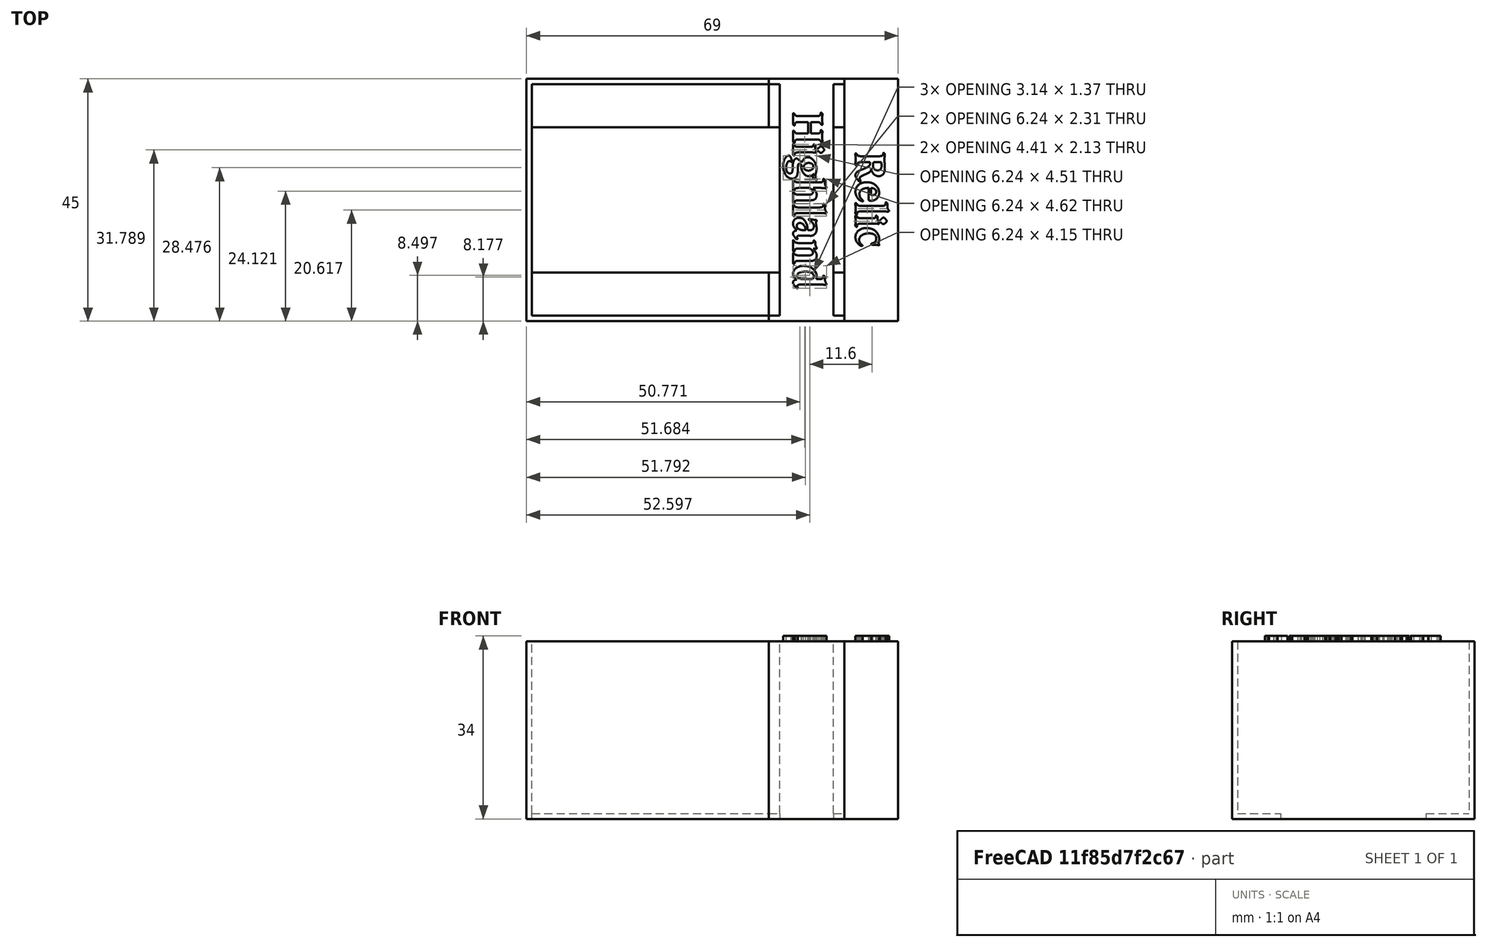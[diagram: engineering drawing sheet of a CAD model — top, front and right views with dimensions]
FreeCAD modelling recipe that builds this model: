
FCSTD DOCUMENT  (FreeCAD 0.18.4R)
Label: test
License: All rights reserved
LicenseURL: http://en.wikipedia.org/wiki/All_rights_reserved
objects: Part::FeaturePython×28, Part::Box×10, Part::MultiFuse×6, Part::Cut×4, Part::Part2DObjectPython×2, Part::Extrusion×2, Part::Feature×2, Part::Plane×2, App::DocumentObjectGroup×2
note: 56 computed .brp shape members not serialized (recipe doc carries the construction recipe); baked Part::Feature solids carry a one-line shape summary decoded from their .brp

FEATURE [Part::Box] Box  label="Cube"
  AttacherType = Attacher::AttachEngine3D
  Height = 33
  Length = 202
  Placement = pos=(0,-1,0) rot=(0,0,1;0rad)
  Width = 45
FEATURE [Part::Box] Box001  label="Cube001"
  AttacherType = Attacher::AttachEngine3D
  Height = 33
  Length = 200
  Placement = pos=(1,0,0) rot=(0,0,1;0rad)
  Width = 43
FEATURE [Part::Cut] Cut
  Base = -> Box
  Tool = -> Box001
FEATURE [Part::Box] Box002  label="Cube002"
  AttacherType = Attacher::AttachEngine3D
  Height = 1
  Length = 202
  Width = 8
FEATURE [Part::Box] Box003  label="Cube003"
  AttacherType = Attacher::AttachEngine3D
  Height = 1
  Length = 202
  Placement = pos=(0,35,0) rot=(0,0,1;0rad)
  Width = 8
FEATURE [Part::MultiFuse] Fusion
  Shapes = -> [Cut,Box002,Box003]
FEATURE [Part::Box] Box004  label="Cube004"
  AttacherType = Attacher::AttachEngine3D
  Height = 33
  Length = 10
  Placement = pos=(47,0,0) rot=(0,0,1;0rad)
  Width = 43
FEATURE [Part::Box] Box005  label="Cube005"
  AttacherType = Attacher::AttachEngine3D
  Height = 33
  Length = 10
  Placement = pos=(60,0,0) rot=(0,0,1;0rad)
  Width = 43
FEATURE [Part::Box] Box006  label="Cube006"
  AttacherType = Attacher::AttachEngine3D
  Height = 33
  Length = 141
  Placement = pos=(61,-1,0) rot=(0,0,1;0rad)
  Width = 45
FEATURE [Part::MultiFuse] Fusion001
  Shapes = -> [Fusion,Box004,Box005]
FEATURE [Part::Cut] Cut001
  Base = -> Fusion001
  Tool = -> Box006
FEATURE [Part::Box] Box007  label="Cube007"
  AttacherType = Attacher::AttachEngine3D
  Height = 33
  Length = 10
  Placement = pos=(59,-1,0) rot=(0,0,1;0rad)
  Width = 45
FEATURE [Part::MultiFuse] Fusion002
  Shapes = -> [Cut001,Box007]
FEATURE [Part::Part2DObjectPython] ShapeString  # Draft 2D object (typed FeaturePython)
  FontFile = <userpath>/Downloads/talisman/Caxton Bold.otf
  Placement = pos=(50.19,26.13,33) rot=(0,0,1;0rad)
  Size = 3
  String = Highland
  Tracking = 0
FEATURE [Part::Part2DObjectPython] ShapeString001  # Draft 2D object (typed FeaturePython)
  FontFile = <userpath>/Downloads/talisman/Caxton Bold.otf
  Placement = pos=(52.65,7.23,33) rot=(0,0,1;0rad)
  Size = 3
  String = Relic
  Tracking = 0
FEATURE [Part::Extrusion] Extrude
  Base = -> ShapeString
  Dir = (0,0,1)
  DirMode = 2
  FaceMakerClass = Part::FaceMakerBullseye
  LengthFwd = 1
  LengthRev = 0
  Placement = pos=(23.5,88,0) rot=(0,0,-1;1.5708rad)
  Solid = false
  Symmetric = false
FEATURE [Part::Extrusion] Extrude001
  Base = -> ShapeString001
  Dir = (0,0,1)
  DirMode = 2
  FaceMakerClass = Part::FaceMakerBullseye
  LengthFwd = 1
  LengthRev = 0
  Placement = pos=(54,83,0) rot=(0,0,-1;1.5708rad)
  Solid = false
  Symmetric = false
FEATURE [Part::MultiFuse] Fusion003
  Shapes = -> [Extrude001,Extrude,Fusion002]
FEATURE [Part::Feature] Fusion003001  label="Fusion004"
  shape: bbox 69 x 45 x 34 mm, 374 faces (baked)
FEATURE [Part::Plane] Plane001
  AttacherType = Attacher::AttachEngine3D
  Length = 100
  Placement = pos=(-10,-10,33) rot=(0,0,1;0rad)
  Width = 100
FEATURE [Part::FeaturePython] Slice  # WARN: FeaturePython — macro-defined, semantics opaque (R4)
  Base = -> Fusion003001
  Mode = 1
  Tolerance = 0
  Tools = -> [Plane001]
FEATURE [Part::FeaturePython] Slice_child0  label="Slice.0"  # WARN: FeaturePython — macro-defined, semantics opaque (R4)
  Base = -> Slice
  FilterType = 1
  Invert = false
  OverrideMaxVal = 0
  WindowFrom = 80
  WindowTo = 100
  items = 0
FEATURE [Part::FeaturePython] Slice_child1  label="Slice.1"  # WARN: FeaturePython — macro-defined, semantics opaque (R4)
  Base = -> Slice
  FilterType = 1
  Invert = false
  OverrideMaxVal = 0
  WindowFrom = 80
  WindowTo = 100
  items = 1
FEATURE [Part::FeaturePython] Slice_child2  label="Slice.2"  # WARN: FeaturePython — macro-defined, semantics opaque (R4)
  Base = -> Slice
  FilterType = 1
  Invert = false
  OverrideMaxVal = 0
  WindowFrom = 80
  WindowTo = 100
  items = 2
FEATURE [Part::FeaturePython] Slice_child3  label="Slice.3"  # WARN: FeaturePython — macro-defined, semantics opaque (R4)
  Base = -> Slice
  FilterType = 1
  Invert = false
  OverrideMaxVal = 0
  WindowFrom = 80
  WindowTo = 100
  items = 3
FEATURE [Part::FeaturePython] Slice_child4  label="Slice.4"  # WARN: FeaturePython — macro-defined, semantics opaque (R4)
  Base = -> Slice
  FilterType = 1
  Invert = false
  OverrideMaxVal = 0
  WindowFrom = 80
  WindowTo = 100
  items = 4
FEATURE [Part::FeaturePython] Slice_child5  label="Slice.5"  # WARN: FeaturePython — macro-defined, semantics opaque (R4)
  Base = -> Slice
  FilterType = 1
  Invert = false
  OverrideMaxVal = 0
  WindowFrom = 80
  WindowTo = 100
  items = 5
FEATURE [Part::FeaturePython] Slice_child6  label="Slice.6"  # WARN: FeaturePython — macro-defined, semantics opaque (R4)
  Base = -> Slice
  FilterType = 1
  Invert = false
  OverrideMaxVal = 0
  WindowFrom = 80
  WindowTo = 100
  items = 6
FEATURE [Part::FeaturePython] Slice_child7  label="Slice.7"  # WARN: FeaturePython — macro-defined, semantics opaque (R4)
  Base = -> Slice
  FilterType = 1
  Invert = false
  OverrideMaxVal = 0
  WindowFrom = 80
  WindowTo = 100
  items = 7
FEATURE [Part::FeaturePython] Slice_child8  label="Slice.8"  # WARN: FeaturePython — macro-defined, semantics opaque (R4)
  Base = -> Slice
  FilterType = 1
  Invert = false
  OverrideMaxVal = 0
  WindowFrom = 80
  WindowTo = 100
  items = 8
FEATURE [Part::FeaturePython] Slice_child9  label="Slice.9"  # WARN: FeaturePython — macro-defined, semantics opaque (R4)
  Base = -> Slice
  FilterType = 1
  Invert = false
  OverrideMaxVal = 0
  WindowFrom = 80
  WindowTo = 100
  items = 9
FEATURE [Part::FeaturePython] Slice_child10  label="Slice.10"  # WARN: FeaturePython — macro-defined, semantics opaque (R4)
  Base = -> Slice
  FilterType = 1
  Invert = false
  OverrideMaxVal = 0
  WindowFrom = 80
  WindowTo = 100
  items = 10
FEATURE [Part::FeaturePython] Slice_child11  label="Slice.11"  # WARN: FeaturePython — macro-defined, semantics opaque (R4)
  Base = -> Slice
  FilterType = 1
  Invert = false
  OverrideMaxVal = 0
  WindowFrom = 80
  WindowTo = 100
  items = 11
FEATURE [Part::FeaturePython] Slice_child12  label="Slice.12"  # WARN: FeaturePython — macro-defined, semantics opaque (R4)
  Base = -> Slice
  FilterType = 1
  Invert = false
  OverrideMaxVal = 0
  WindowFrom = 80
  WindowTo = 100
  items = 12
FEATURE [Part::FeaturePython] Slice_child13  label="Slice.13"  # WARN: FeaturePython — macro-defined, semantics opaque (R4)
  Base = -> Slice
  FilterType = 1
  Invert = false
  OverrideMaxVal = 0
  WindowFrom = 80
  WindowTo = 100
  items = 13
FEATURE [Part::FeaturePython] Slice_child14  label="Slice.14"  # WARN: FeaturePython — macro-defined, semantics opaque (R4)
  Base = -> Slice
  FilterType = 1
  Invert = false
  OverrideMaxVal = 0
  WindowFrom = 80
  WindowTo = 100
  items = 14
FEATURE [Part::FeaturePython] Slice_child15  label="Slice.15"  # WARN: FeaturePython — macro-defined, semantics opaque (R4)
  Base = -> Slice
  FilterType = 1
  Invert = false
  OverrideMaxVal = 0
  WindowFrom = 80
  WindowTo = 100
  items = 15
FEATURE [Part::MultiFuse] Fusion003002
  Shapes = -> [Slice_child1,Slice_child3,Slice_child5,Slice_child4,Slice_child2,Slice_child14,Slice_child6,Slice_child13,Slice_child8,Slice_child7,Slice_child10,Slice_child11,Slice_child9,Slice_child15,Slice_child12]
FEATURE [App::DocumentObjectGroup] GrExplode_Slice  label="Exploded Slice"
  Group = -> [Slice_child0,Fusion003002]
FEATURE [Part::Feature] Fusion003003
  shape: bbox 69 x 45 x 34 mm, 406 faces (baked)
FEATURE [Part::Box] Box008  label="Cube008"
  AttacherType = Attacher::AttachEngine3D
  Height = 40
  Length = 100
  Placement = pos=(-55,-10,-4) rot=(0,0,1;0rad)
  Width = 100
FEATURE [Part::Box] Box009  label="Cube009"
  AttacherType = Attacher::AttachEngine3D
  Height = 40
  Length = 100
  Placement = pos=(59,-10,-4) rot=(0,0,1;0rad)
  Width = 100
FEATURE [Part::Cut] Cut002
  Base = -> Fusion003003
  Tool = -> Box008
FEATURE [Part::Cut] Cut003
  Base = -> Cut002
  Tool = -> Box009
FEATURE [Part::Plane] Plane
  AttacherType = Attacher::AttachEngine3D
  Length = 100
  Placement = pos=(0,-23,33) rot=(0,0,1;0rad)
  Width = 100
FEATURE [Part::FeaturePython] Slice001  # WARN: FeaturePython — macro-defined, semantics opaque (R4)
  Base = -> Cut003
  Mode = 1
  Tolerance = 0
  Tools = -> [Plane]
FEATURE [Part::FeaturePython] Slice001_child0  label="pieza"  # WARN: FeaturePython — macro-defined, semantics opaque (R4)
  Base = -> Slice001
  FilterType = 1
  Invert = false
  OverrideMaxVal = 0
  WindowFrom = 80
  WindowTo = 100
  items = 0
FEATURE [Part::FeaturePython] Slice001_child1  label="Slice001.1"  # WARN: FeaturePython — macro-defined, semantics opaque (R4)
  Base = -> Slice001
  FilterType = 1
  Invert = false
  OverrideMaxVal = 0
  WindowFrom = 80
  WindowTo = 100
  items = 1
FEATURE [Part::FeaturePython] Slice001_child2  label="Slice001.2"  # WARN: FeaturePython — macro-defined, semantics opaque (R4)
  Base = -> Slice001
  FilterType = 1
  Invert = false
  OverrideMaxVal = 0
  WindowFrom = 80
  WindowTo = 100
  items = 2
FEATURE [Part::FeaturePython] Slice001_child3  label="Slice001.3"  # WARN: FeaturePython — macro-defined, semantics opaque (R4)
  Base = -> Slice001
  FilterType = 1
  Invert = false
  OverrideMaxVal = 0
  WindowFrom = 80
  WindowTo = 100
  items = 3
FEATURE [Part::FeaturePython] Slice001_child4  label="Slice001.4"  # WARN: FeaturePython — macro-defined, semantics opaque (R4)
  Base = -> Slice001
  FilterType = 1
  Invert = false
  OverrideMaxVal = 0
  WindowFrom = 80
  WindowTo = 100
  items = 4
FEATURE [Part::FeaturePython] Slice001_child5  label="Slice001.5"  # WARN: FeaturePython — macro-defined, semantics opaque (R4)
  Base = -> Slice001
  FilterType = 1
  Invert = false
  OverrideMaxVal = 0
  WindowFrom = 80
  WindowTo = 100
  items = 5
FEATURE [Part::FeaturePython] Slice001_child6  label="Slice001.6"  # WARN: FeaturePython — macro-defined, semantics opaque (R4)
  Base = -> Slice001
  FilterType = 1
  Invert = false
  OverrideMaxVal = 0
  WindowFrom = 80
  WindowTo = 100
  items = 6
FEATURE [Part::FeaturePython] Slice001_child7  label="Slice001.7"  # WARN: FeaturePython — macro-defined, semantics opaque (R4)
  Base = -> Slice001
  FilterType = 1
  Invert = false
  OverrideMaxVal = 0
  WindowFrom = 80
  WindowTo = 100
  items = 7
FEATURE [Part::FeaturePython] Slice001_child8  label="Slice001.8"  # WARN: FeaturePython — macro-defined, semantics opaque (R4)
  Base = -> Slice001
  FilterType = 1
  Invert = false
  OverrideMaxVal = 0
  WindowFrom = 80
  WindowTo = 100
  items = 8
FEATURE [Part::FeaturePython] Slice001_child9  label="Slice001.9"  # WARN: FeaturePython — macro-defined, semantics opaque (R4)
  Base = -> Slice001
  FilterType = 1
  Invert = false
  OverrideMaxVal = 0
  WindowFrom = 80
  WindowTo = 100
  items = 9
FEATURE [Part::MultiFuse] Fusion003004  label="letras"
  Shapes = -> [Slice001_child1,Slice001_child9,Slice001_child8,Slice001_child3,Slice001_child4,Slice001_child5,Slice001_child2,Slice001_child6,Slice001_child7]
FEATURE [App::DocumentObjectGroup] GrExplode_Slice001  label="Exploded Slice001"
  Group = -> [Slice001_child0,Fusion003004]
